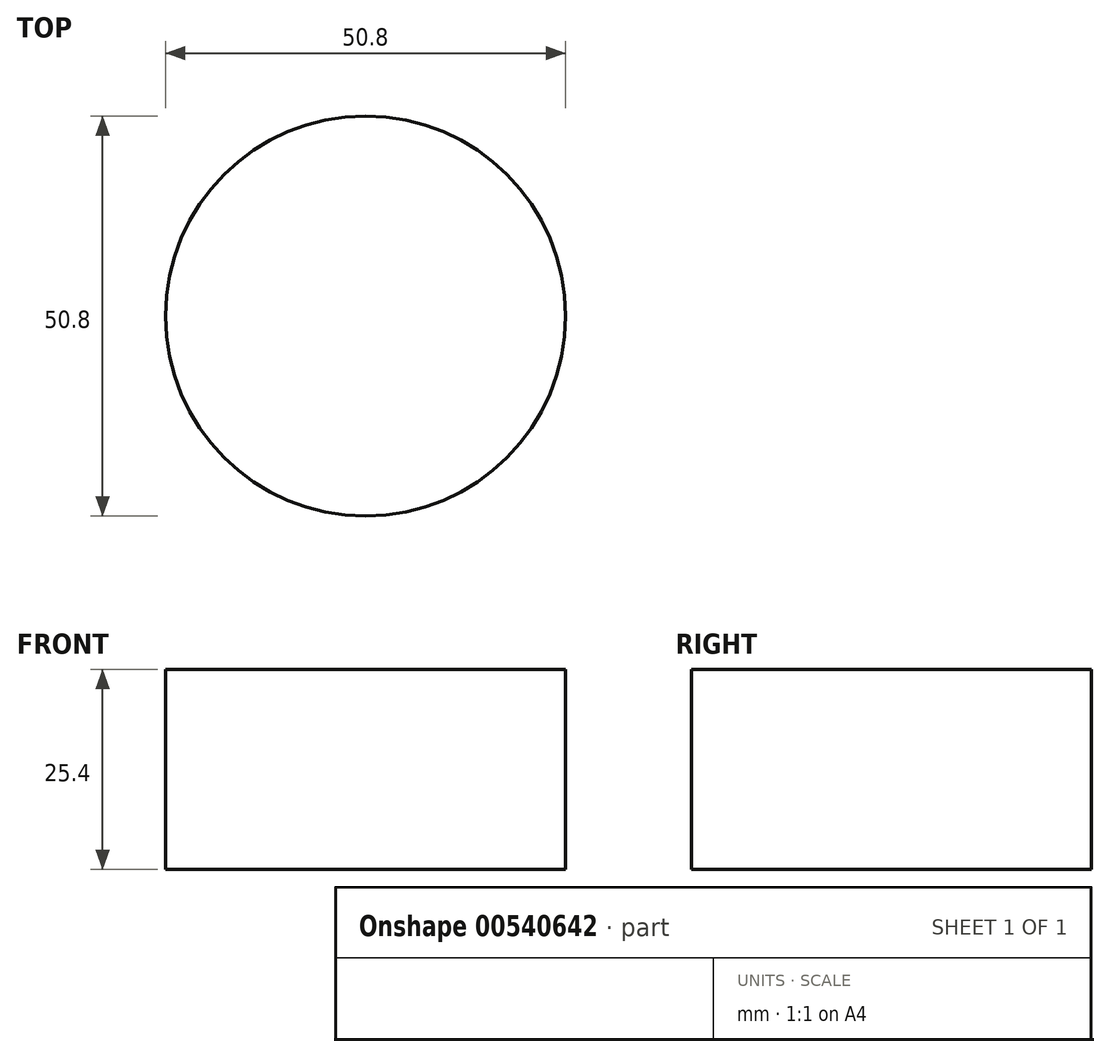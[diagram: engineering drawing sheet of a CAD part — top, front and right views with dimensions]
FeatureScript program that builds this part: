
annotation { "Feature Type Name" : "Feature", "Feature Type Description" : "" }
export const myFeature = defineFeature(function(context is Context, id is Id, definition is map)
    precondition{}
    {
        {
            var Q0;
            Q0=qCreatedBy(makeId("Top.planeOp"),FACE);
            cPlane(context, id + "F0", {"entities" : qUnion([Q0]), "cplaneType" : CPlaneType.OFFSET, "offset" : 50.8 * mm, "width" : 152.4 * mm, "height" : 152.4 * mm});
        }
        {
            var Q0;
            Q0=qCreatedBy(id+"F0.planeOp",FACE);
            cPlane(context, id + "F1", {"entities" : qUnion([Q0]), "cplaneType" : CPlaneType.OFFSET, "offset" : 101.6 * mm, "width" : 152.4 * mm, "height" : 152.4 * mm});
        }
        {
            var Q0;
            Q0=qCreatedBy(id+"F0.planeOp",FACE);
            var sketch = newSketch(context, id + "F2", { "sketchPlane" : qUnion([Q0])});
            skCircle(sketch, "E0.0", {"center": v(0, 0) * mm, "radius": 25.4 * mm});
            skSolve(sketch);
        }
        {
            var Q0;
            Q0=qCreatedBy(id+"F1.planeOp",FACE);
            var sketch = newSketch(context, id + "F3", { "sketchPlane" : qUnion([Q0])});
            skCircle(sketch, "E1.0", {"center": v(0, 0) * mm, "radius": 25.4 * mm});
            skSolve(sketch);
        }
        {
            var Q0;
            Q0=makeQuery(id+"F3.imprint","IMPRINT",FACE,{"disambiguationData":[TD([[makeQuery(id+"F3.imprint","IMPRINT",EDGE,{"derivedFrom":sQuery(id+"F3.wireOp",EDGE,"E1.0")}),1.0]])]});
            extrude(context, id + "F4", {"entities" : qUnion([Q0]), "depth" : 25.4 * mm, "offsetDistance" : 25.4 * mm});
        }
    });
